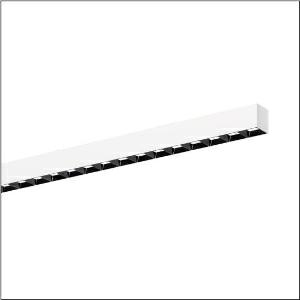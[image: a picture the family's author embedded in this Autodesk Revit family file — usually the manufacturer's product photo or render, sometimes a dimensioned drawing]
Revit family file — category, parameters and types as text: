
# Revit family: silica_r__21_51mx21tbt5w_e527
name_source: partatom
category: Lighting Fixtures
units: mm (PartAtom-declared; Revit-internal decimal feet)

## family parameters
Cut with Voids When Loaded = No
Host = Face
Light Source = No
Part Type = Normal
Room Calculation Point = No
Round Connector Dimension = Use Diameter
Shared = No

## types (1)
- --- (1 x LED, 4650 lm, 40.3 W, 6500K)
    Apparent Load = 40 VA
    CIE Flux Codes = 85 99 100 100 100
    Color Rendering = 80
    Color Temperature = 6500K
    Default Elevation = 1800 mm
    Description = Silica® 21, office luminaire, primary light control with darklight reflector, of PMMA, black, CAT 2 (L<= 3000cd/m²), light emission: direct distribution, primary light characteristic: symmetric, installation type: surface-mounted, LED, rated luminous flux: 4.650lm, luminous efficacy: 110lm/W, light colour: 8tw, colour temperature: 2700..6500K, control gear: ECG DALI, with terminal, 3+2-pole, max. 2.5mm², mains connection: 220..240V, AC, 50/60Hz, rated input power: 42.3W, luminaire housing, of aluminium, traffic white (RAL 9016), length: 1.504mm, width: 53mm, height: 53mm, protection rating (complete): IP20, insulation class (complete): insulation class I (protective earthing), certification: CE, permissible operating ambient temperature: 0..+35°C, standard: EN 50419, packaging unit: 1 piece
    Height = 0 mm  [stored 0 ft]
    Lamp = 1 x LED
    Lamp Light Flux = 4650 lm
    Lamp Power = 40.3 W
    Lamp count = 1
    Length = 1504 mm
    Luminous efficacy = 115 lm/W
    Manufacturer = Siteco
    ModVariant = No
    Model = 51MX21TBT5W
    Mounting Place = Ceiling
    Mounting Type = Recessed
    Number of Poles = 1
    OnlyDefault = Yes
    Power Factor = 1
    Product Name = Silica® 21
    Product group = office luminaire | ceiling recessed
    ProductGroupID = 400
    Protection Class = Protection class I
    Protection Degree = IP 20
    RLX_Detail_Level = 1
    RLX_Emergency_Light_Flux = 0 lm
    RLX_Emergency_Type = 0
    RLX_Emergency_Type_DB = No
    RlxData = <blob elided: 41029 chars, md5=3805994e>
    Socket = socket
    Standby Power = 0 W
    System Light Flux = 4650 lm
    System Power = 40 W
    Type Comments = individual setting
    Type Image = l_1335873.jpg
    URL = http://relux.com
    VarID = @adj_109885
    Voltage = 0 V
    Weight = 0.00 kg
    Width = 53 mm

note: [stored X ft] marks values corroborated as IEEE doubles in the binary element streams (Revit-internal decimal feet)

## geometry (parser evidence)
native form markers: Blend x4, Sweep x9
no freeform markers — native parametric forms only
